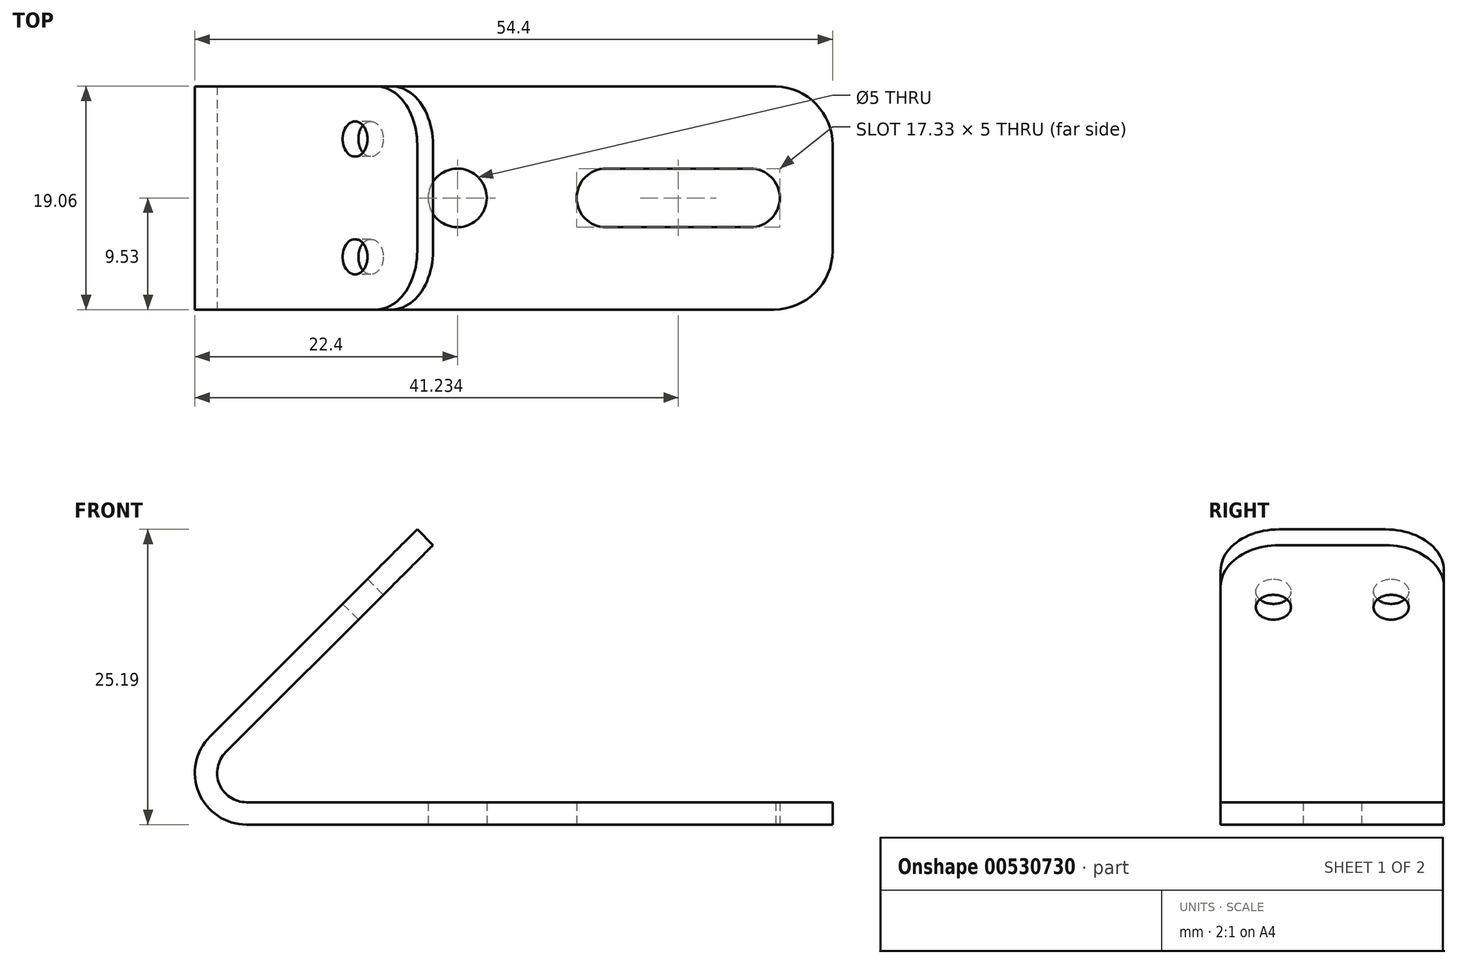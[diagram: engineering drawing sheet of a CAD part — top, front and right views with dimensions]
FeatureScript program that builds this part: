
annotation { "Feature Type Name" : "Feature", "Feature Type Description" : "" }
export const myFeature = defineFeature(function(context is Context, id is Id, definition is map)
    precondition{}
    {
        {
            var Q0;
            Q0=qCreatedBy(makeId("Front.planeOp"),FACE);
            var sketch = newSketch(context, id + "F0", { "sketchPlane" : qUnion([Q0])});
            skArc(sketch, "E0", {"start": v(-3.11, 7.51) * mm, "mid": v(-4.07, 2.72) * mm, "end": v(0, 0) * mm});
            skArc(sketch, "E1", {"start": v(-1.77, 6.17) * mm, "mid": v(-2.3, 3.44) * mm, "end": v(0, 1.9) * mm});
            skLineSegment(sketch, "E2.bottom", {"start": v(0, 0) * mm, "end": v(50, 0) * mm});
            skLineSegment(sketch, "E2.top", {"start": v(0, 1.9) * mm, "end": v(50, 1.9) * mm});
            skLineSegment(sketch, "E2.right", {"start": v(50, 0) * mm, "end": v(50, 1.9) * mm});
            skLineSegment(sketch, "E3", {"start": v(-3.11, 7.51) * mm, "end": v(14.57, 25.19) * mm});
            skLineSegment(sketch, "E4", {"start": v(14.57, 25.19) * mm, "end": v(15.9, 23.85) * mm});
            skLineSegment(sketch, "E5", {"start": v(15.9, 23.85) * mm, "end": v(-1.77, 6.17) * mm});
            skSolve(sketch);
        }
        {
            var Q0;
            Q0=qCreatedBy(makeId("Top.planeOp"),FACE);
            var sketch = newSketch(context, id + "F1", { "sketchPlane" : qUnion([Q0])});
            skLineSegment(sketch, "E6.bottom", {"start": v(45, 9.52) * mm, "end": v(0, 9.52) * mm, "construction": true});
            skLineSegment(sketch, "E6.top", {"start": v(45, -9.53) * mm, "end": v(0, -9.53) * mm, "construction": true});
            skLineSegment(sketch, "E6.left", {"start": v(50, 4.53) * mm, "end": v(50, -4.52) * mm, "construction": true});
            skLineSegment(sketch, "E6.right", {"start": v(0, 9.52) * mm, "end": v(0, -9.53) * mm});
            skPoint(sketch, "E6.middle", {"position": v(25, 0) * mm});
            skCircle(sketch, "E7", {"center": v(18, 0) * mm, "radius": 2.5 * mm});
            skPoint(sketch, "E7.centerSnap0", {"position": v(0, 0) * mm});
            skArc(sketch, "E8", {"start": v(30.67, 2.5) * mm, "mid": v(28.9, 1.77) * mm, "end": v(28.17, 0) * mm});
            skArc(sketch, "E9", {"start": v(43, -2.5) * mm, "mid": v(44.77, -1.77) * mm, "end": v(45.5, 0) * mm});
            skLineSegment(sketch, "E10", {"start": v(30.67, 2.5) * mm, "end": v(43, 2.5) * mm});
            skLineSegment(sketch, "E11", {"start": v(30.67, -2.5) * mm, "end": v(43, -2.5) * mm});
            skArc(sketch, "E12", {"start": v(28.17, 0) * mm, "mid": v(28.9, -1.77) * mm, "end": v(30.67, -2.5) * mm});
            skArc(sketch, "E13", {"start": v(45.5, 0) * mm, "mid": v(44.77, 1.77) * mm, "end": v(43, 2.5) * mm});
            skPoint(sketch, "E14.visualSharp", {"position": v(50, 9.52) * mm});
            skArc(sketch, "E14.filletArc", {"start": v(50, 4.53) * mm, "mid": v(48.54, 8.06) * mm, "end": v(45, 9.53) * mm});
            skPoint(sketch, "E15.visualSharp", {"position": v(50, -9.53) * mm});
            skArc(sketch, "E15.filletArc", {"start": v(45, -9.52) * mm, "mid": v(48.54, -8.06) * mm, "end": v(50, -4.52) * mm});
            skLineSegment(sketch, "E16", {"start": v(50, 4.53) * mm, "end": v(50, 9.52) * mm});
            skLineSegment(sketch, "E17", {"start": v(45.17, 9.52) * mm, "end": v(50, 9.52) * mm});
            skLineSegment(sketch, "E18", {"start": v(50, -4.52) * mm, "end": v(50, -9.53) * mm});
            skLineSegment(sketch, "E19", {"start": v(45, -9.53) * mm, "end": v(50, -9.53) * mm});
            skSolve(sketch);
        }
        {
            var Q0;
            Q0=sQuery(id+"F0.wireOp",EDGE,"E3");
            cPlane(context, id + "F2", {"entities" : qUnion([Q0]), "cplaneType" : CPlaneType.LINE_ANGLE, "offset" : 25 * mm, "angle" : 90 * degree, "width" : 150 * mm, "height" : 150 * mm});
        }
        {
            var Q0;
            Q0=qCreatedBy(id+"F2.planeOp",FACE);
            var sketch = newSketch(context, id + "F3", { "sketchPlane" : qUnion([Q0])});
            skPoint(sketch, "E20.0", {"position": v(-9.52, 15.9) * mm});
            skLineSegment(sketch, "E21.bottom", {"start": v(-9.52, 28.11) * mm, "end": v(-4.53, 28.11) * mm});
            skLineSegment(sketch, "E21.left", {"start": v(-9.52, 28.11) * mm, "end": v(-9.52, 23.11) * mm});
            skLineSegment(sketch, "E21.right", {"start": v(9.52, 28.11) * mm, "end": v(9.52, 23.11) * mm});
            skPoint(sketch, "E21.middle", {"position": v(0, 15.61) * mm});
            skPoint(sketch, "E22.visualSharp", {"position": v(-9.52, 28.11) * mm});
            skArc(sketch, "E22.filletArc", {"start": v(-4.53, 28.11) * mm, "mid": v(-8.06, 26.65) * mm, "end": v(-9.52, 23.11) * mm});
            skPoint(sketch, "E23.visualSharp", {"position": v(9.52, 28.11) * mm});
            skArc(sketch, "E23.filletArc", {"start": v(9.52, 23.11) * mm, "mid": v(8.06, 26.65) * mm, "end": v(4.52, 28.11) * mm});
            skLineSegment(sketch, "E24", {"start": v(4.52, 23.11) * mm, "end": v(4.52, 35.36) * mm, "construction": true});
            skLineSegment(sketch, "E25", {"start": v(-4.53, 23.11) * mm, "end": v(-4.53, 35.36) * mm, "construction": true});
            skCircle(sketch, "E26", {"center": v(-5.02, 20.61) * mm, "radius": 1.5 * mm});
            skCircle(sketch, "E27.MirrorC", {"center": v(5.02, 20.61) * mm, "radius": 1.5 * mm});
            skPoint(sketch, "E21.top.start.orphan", {"position": v(-9.52, 3.11) * mm});
            skPoint(sketch, "E28.orphan", {"position": v(9.53, 3.11) * mm});
            skLineSegment(sketch, "E29.trimOffspring", {"start": v(4.52, 28.11) * mm, "end": v(9.52, 28.11) * mm});
            skLineSegment(sketch, "E30", {"start": v(-4.53, 28.11) * mm, "end": v(0, 28.11) * mm, "construction": true});
            skLineSegment(sketch, "E31", {"start": v(0, 28.11) * mm, "end": v(4.52, 28.11) * mm, "construction": true});
            skSolve(sketch);
        }
        {
            var Q0;
            Q0=makeQuery(id+"F0.imprint","IMPRINT",FACE,{"disambiguationData":[TD([[makeQuery(id+"F0.imprint","IMPRINT",EDGE,{"derivedFrom":sQuery(id+"F0.wireOp",EDGE,"E0")}),1.0]])]});
            var Q1;
            Q1=sQuery(id+"F1.wireOp",VERTEX,"E6.right.start");
            var Q2;
            Q2=sQuery(id+"F1.wireOp",VERTEX,"E6.right.end");
            extrude(context, id + "F4", {"entities" : qUnion([Q0]), "endBound" : BoundingType.UP_TO_VERTEX, "oppositeDirection" : true, "endBoundEntityVertex" : qUnion([Q1]), "depth" : 39.62 * mm, "hasSecondDirection" : true, "secondDirectionBound" : SecondDirectionBoundingType.UP_TO_VERTEX, "secondDirectionOppositeDirection" : false, "secondDirectionBoundEntityVertex" : qUnion([Q2]), "secondDirectionDepth" : 25 * mm});
        }
        {
            var Q0;
            Q0=qSketchRegion(id+"F1",true);
            var Q1;
            Q1=sQuery(id+"F0.wireOp",VERTEX,"E2.right.end");
            extrude(context, id + "F5", {"entities" : qUnion([Q0]), "operationType" : NewBodyOperationType.REMOVE, "endBound" : BoundingType.UP_TO_VERTEX, "endBoundEntityVertex" : qUnion([Q1]), "depth" : 25 * mm});
        }
        {
            var Q0;
            Q0=qSketchRegion(id+"F3",true);
            var Q1;
            Q1=sQuery(id+"F0.wireOp",VERTEX,"E5.start");
            extrude(context, id + "F6", {"entities" : qUnion([Q0]), "operationType" : NewBodyOperationType.REMOVE, "endBound" : BoundingType.UP_TO_VERTEX, "oppositeDirection" : true, "endBoundEntityVertex" : qUnion([Q1]), "depth" : 25 * mm});
        }
    });
